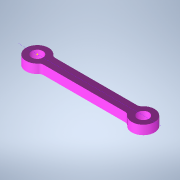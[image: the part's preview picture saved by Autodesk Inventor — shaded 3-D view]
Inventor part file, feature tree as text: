
AUTODESK INVENTOR PART (.ipt)
format: ipt  version: 2022 (Build 260153000, 153)  size: 112,128 bytes
history: imported  units: in
note: dims shown in document units (in); Inventor stores cm internally (conversion verified against a paired STEP export)
features: sketch x1, imported_body x1
ambient origin geometry x8: Origin, YZ Plane, XZ Plane, XY Plane, X Axis, Y Axis, Z Axis, Center Point
bodies: Solid1 (imported_parasolid), Body1 (imported_parasolid)
feature tree (2):
  sketch  "Sketch1"
  imported_body  NMx_Import_Brep_tag  [imported B-rep: ~12 faces, bbox_mm=[140.0, 12.0, 19.58831]]
